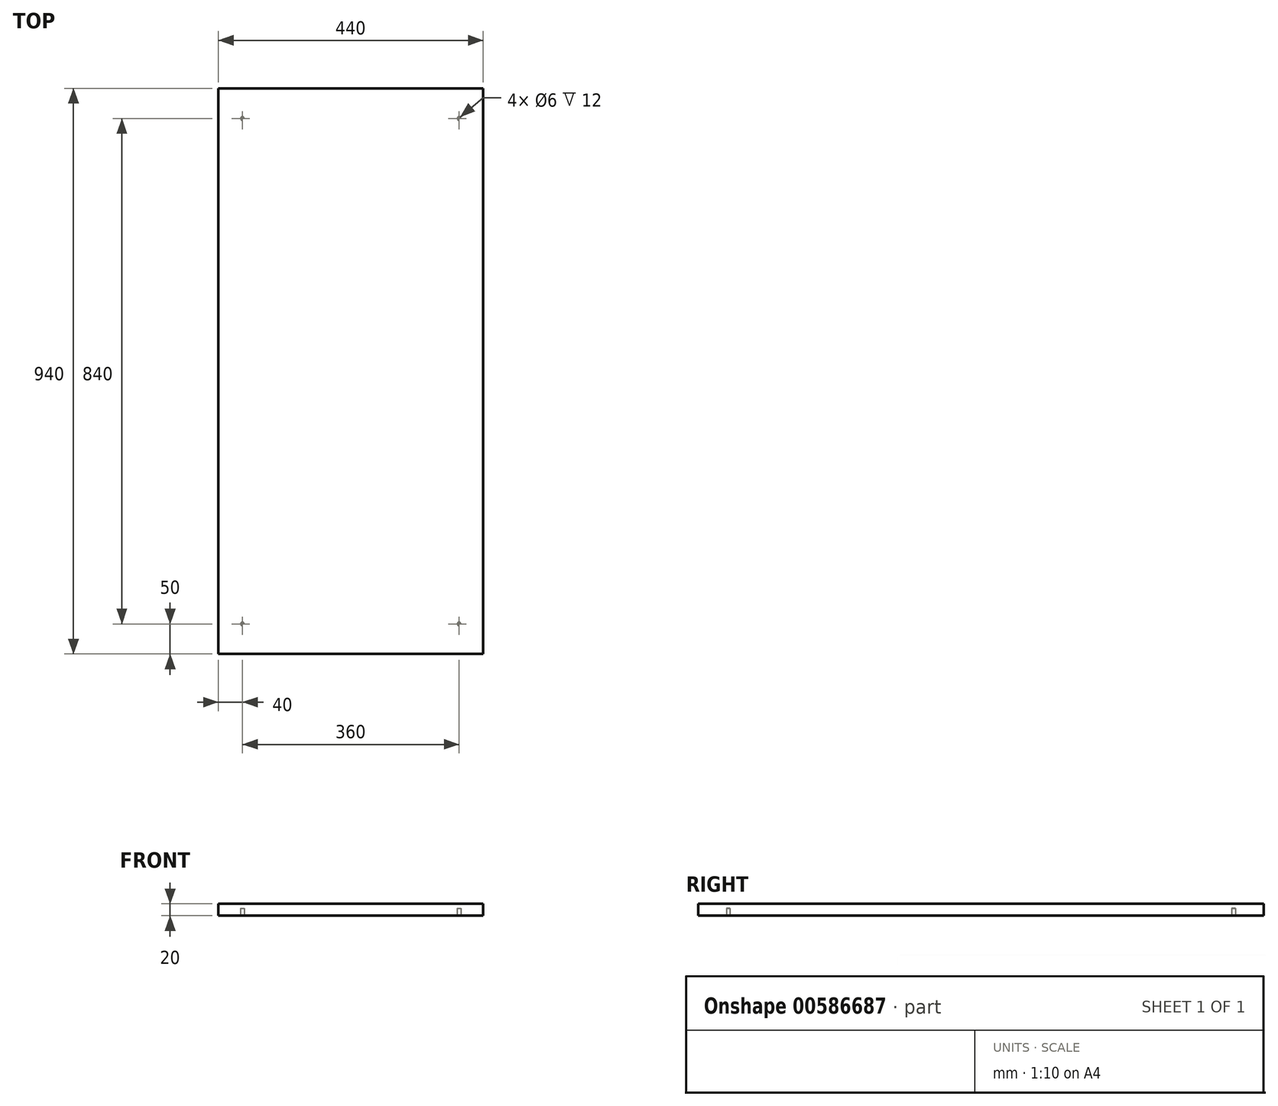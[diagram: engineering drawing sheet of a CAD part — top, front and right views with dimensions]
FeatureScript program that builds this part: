
annotation { "Feature Type Name" : "Feature", "Feature Type Description" : "" }
export const myFeature = defineFeature(function(context is Context, id is Id, definition is map)
    precondition{}
    {
        {
            var Q0;
            Q0=qCreatedBy(makeId("Front.planeOp"),FACE);
            var sketch = newSketch(context, id + "F0", { "sketchPlane" : qUnion([Q0])});
            skLineSegment(sketch, "E0.bottom", {"start": v(0, 0) * mm, "end": v(-440, 0) * mm});
            skLineSegment(sketch, "E0.top", {"start": v(0, 20) * mm, "end": v(-440, 20) * mm});
            skLineSegment(sketch, "E0.left", {"start": v(0, 0) * mm, "end": v(0, 20) * mm});
            skLineSegment(sketch, "E0.right", {"start": v(-440, 0) * mm, "end": v(-440, 20) * mm});
            skSolve(sketch);
        }
        {
            var Q0;
            Q0 = qSketchRegion(id + "F0", true);
            extrude(context, id + "F1", {"entities" : qUnion([Q0]), "depth" : 940 * mm, "offsetDistance" : 25 * mm, "symmetric" : true});
        }
        {
            var Q0;
            Q0=makeQuery(id+"F1.opExtrude","SWEPT_FACE",FACE,{"disambiguationData":[OSD([sQuery(id+"F0.wireOp",EDGE,"E0.bottom")])]});
            var sketch = newSketch(context, id + "F2", { "sketchPlane" : qUnion([Q0])});
            skCircle(sketch, "E1", {"center": v(-400, 420) * mm, "radius": 3 * mm});
            skSolve(sketch);
        }
        {
            var Q0;
            Q0 = qSketchRegion(id + "F2", true);
            extrude(context, id + "F3", {"entities" : qUnion([Q0]), "operationType" : NewBodyOperationType.REMOVE, "oppositeDirection" : true, "depth" : 12 * mm, "offsetDistance" : 25 * mm});
        }
        {
            var Q0;
            Q0=makeQuery(id+"F1.opExtrude","SWEPT_FACE",FACE,{"disambiguationData":[OSD([sQuery(id+"F0.wireOp",EDGE,"E0.bottom")])]});
            var sketch = newSketch(context, id + "F4", { "sketchPlane" : qUnion([Q0])});
            skCircle(sketch, "E2", {"center": v(-40, 420) * mm, "radius": 3 * mm});
            skSolve(sketch);
        }
        {
            var Q0;
            Q0 = qSketchRegion(id + "F4", true);
            extrude(context, id + "F5", {"entities" : qUnion([Q0]), "operationType" : NewBodyOperationType.REMOVE, "oppositeDirection" : true, "depth" : 12 * mm, "offsetDistance" : 25 * mm});
        }
        {
            var Q0;
            Q0=makeQuery(id+"F1.opExtrude","SWEPT_FACE",FACE,{"disambiguationData":[OSD([sQuery(id+"F0.wireOp",EDGE,"E0.bottom")])]});
            var sketch = newSketch(context, id + "F6", { "sketchPlane" : qUnion([Q0])});
            skCircle(sketch, "E3", {"center": v(-400, -420) * mm, "radius": 3 * mm});
            skSolve(sketch);
        }
        {
            var Q0;
            Q0 = qSketchRegion(id + "F6", true);
            extrude(context, id + "F7", {"entities" : qUnion([Q0]), "operationType" : NewBodyOperationType.REMOVE, "oppositeDirection" : true, "depth" : 12 * mm, "offsetDistance" : 25 * mm});
        }
        {
            var Q0;
            Q0=makeQuery(id+"F1.opExtrude","SWEPT_FACE",FACE,{"disambiguationData":[OSD([sQuery(id+"F0.wireOp",EDGE,"E0.bottom")])]});
            var sketch = newSketch(context, id + "F8", { "sketchPlane" : qUnion([Q0])});
            skCircle(sketch, "E4", {"center": v(-40, -420) * mm, "radius": 3 * mm});
            skSolve(sketch);
        }
        {
            var Q0;
            Q0 = qSketchRegion(id + "F8", true);
            extrude(context, id + "F9", {"entities" : qUnion([Q0]), "operationType" : NewBodyOperationType.REMOVE, "oppositeDirection" : true, "depth" : 12 * mm, "offsetDistance" : 25 * mm});
        }
    });
